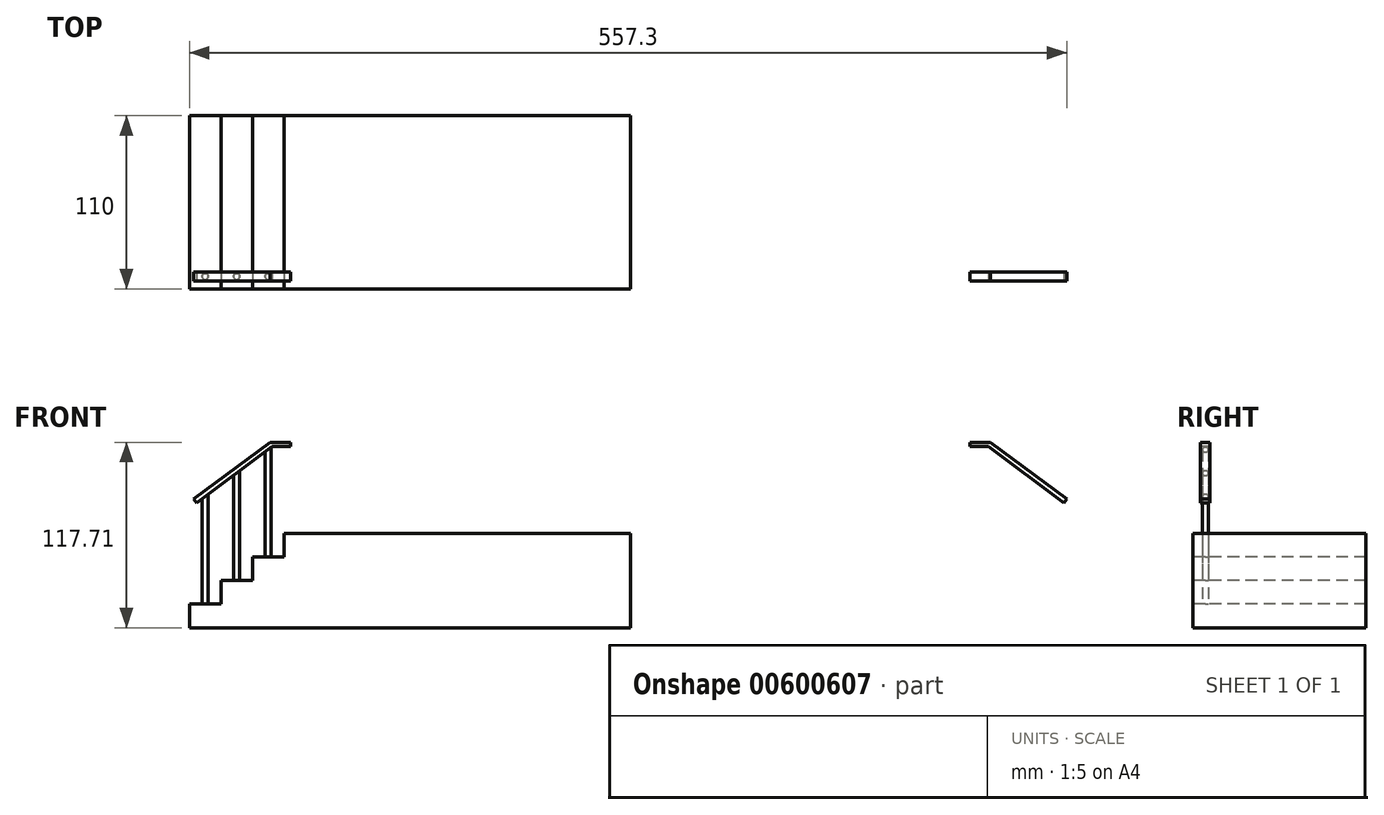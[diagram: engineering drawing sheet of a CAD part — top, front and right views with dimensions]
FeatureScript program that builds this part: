
annotation { "Feature Type Name" : "Feature", "Feature Type Description" : "" }
export const myFeature = defineFeature(function(context is Context, id is Id, definition is map)
    precondition{}
    {
        {
            var Q0;
            Q0=qCreatedBy(makeId("Top.planeOp"),FACE);
            var sketch = newSketch(context, id + "F0", { "sketchPlane" : qUnion([Q0])});
            skLineSegment(sketch, "E0.bottom", {"start": v(-214.98, -22.54) * mm, "end": v(5.02, -22.54) * mm});
            skLineSegment(sketch, "E0.top", {"start": v(-214.98, -132.54) * mm, "end": v(5.02, -132.54) * mm});
            skLineSegment(sketch, "E0.left", {"start": v(-214.98, -22.54) * mm, "end": v(-214.98, -132.54) * mm});
            skLineSegment(sketch, "E0.right", {"start": v(5.02, -22.54) * mm, "end": v(5.02, -132.54) * mm});
            skLineSegment(sketch, "E1.bottom", {"start": v(-214.98, -22.54) * mm, "end": v(-234.98, -22.54) * mm});
            skLineSegment(sketch, "E1.top", {"start": v(-214.98, -132.54) * mm, "end": v(-234.98, -132.54) * mm});
            skLineSegment(sketch, "E1.right", {"start": v(-234.98, -22.54) * mm, "end": v(-234.98, -132.54) * mm});
            skLineSegment(sketch, "E2.bottom", {"start": v(-234.98, -22.54) * mm, "end": v(-254.98, -22.54) * mm});
            skLineSegment(sketch, "E2.top", {"start": v(-234.98, -132.54) * mm, "end": v(-254.98, -132.54) * mm});
            skLineSegment(sketch, "E2.right", {"start": v(-254.98, -22.54) * mm, "end": v(-254.98, -132.54) * mm});
            skLineSegment(sketch, "E3.bottom", {"start": v(-254.98, -22.54) * mm, "end": v(-274.98, -22.54) * mm});
            skLineSegment(sketch, "E3.top", {"start": v(-254.98, -132.54) * mm, "end": v(-274.98, -132.54) * mm});
            skLineSegment(sketch, "E3.right", {"start": v(-274.98, -22.54) * mm, "end": v(-274.98, -132.54) * mm});
            skCircle(sketch, "E4", {"center": v(-264.98, -124.54) * mm, "radius": 2 * mm});
            skPoint(sketch, "E4.centerSnap0", {"position": v(-264.98, -132.54) * mm});
            skCircle(sketch, "E5", {"center": v(-244.98, -124.54) * mm, "radius": 2 * mm});
            skPoint(sketch, "E5.centerSnap0", {"position": v(-244.98, -132.54) * mm});
            skCircle(sketch, "E6", {"center": v(-224.98, -124.54) * mm, "radius": 2 * mm});
            skPoint(sketch, "E6.centerSnap0", {"position": v(-224.98, -132.54) * mm});
            skSolve(sketch);
        }
        {
            var Q0;
            Q0=makeQuery(id+"F0.imprint","IMPRINT",FACE,{"disambiguationData":[TD([[makeQuery(id+"F0.imprint","IMPRINT",EDGE,{"derivedFrom":sQuery(id+"F0.wireOp",EDGE,"E3.bottom")}),1.0]])]});
            extrude(context, id + "F1", {"entities" : qUnion([Q0]), "depth" : 15 * mm, "offsetDistance" : 25 * mm});
        }
        {
            var Q0;
            Q0=makeQuery(id+"F0.imprint","IMPRINT",FACE,{"disambiguationData":[TD([[makeQuery(id+"F0.imprint","IMPRINT",EDGE,{"derivedFrom":sQuery(id+"F0.wireOp",EDGE,"E2.bottom")}),1.0]])]});
            var Q1;
            Q1=makeQuery(id+"F0.imprint","IMPRINT",FACE,{"disambiguationData":[TD([[makeQuery(id+"F0.imprint","IMPRINT",EDGE,{"derivedFrom":sQuery(id+"F0.wireOp",EDGE,"E5")}),1.0]])]});
            extrude(context, id + "F2", {"entities" : qUnion([Q0, Q1]), "operationType" : NewBodyOperationType.ADD, "depth" : 30 * mm, "offsetDistance" : 25 * mm});
        }
        {
            var Q0;
            Q0=makeQuery(id+"F0.imprint","IMPRINT",FACE,{"disambiguationData":[TD([[makeQuery(id+"F0.imprint","IMPRINT",EDGE,{"derivedFrom":sQuery(id+"F0.wireOp",EDGE,"E1.bottom")}),1.0]])]});
            extrude(context, id + "F3", {"entities" : qUnion([Q0]), "operationType" : NewBodyOperationType.ADD, "depth" : 45 * mm, "offsetDistance" : 25 * mm});
        }
        {
            var Q0;
            Q0=makeQuery(id+"F0.imprint","IMPRINT",FACE,{"disambiguationData":[TD([[makeQuery(id+"F0.imprint","IMPRINT",EDGE,{"derivedFrom":sQuery(id+"F0.wireOp",EDGE,"E0.bottom")}),-1.0]])]});
            extrude(context, id + "F4", {"entities" : qUnion([Q0]), "operationType" : NewBodyOperationType.ADD, "depth" : 60 * mm, "offsetDistance" : 25 * mm});
        }
        {
            var Q0;
            Q0=makeQuery(id+"F0.imprint","IMPRINT",FACE,{"disambiguationData":[TD([[makeQuery(id+"F0.imprint","IMPRINT",EDGE,{"derivedFrom":sQuery(id+"F0.wireOp",EDGE,"E4")}),1.0]])]});
            extrude(context, id + "F5", {"entities" : qUnion([Q0]), "operationType" : NewBodyOperationType.ADD, "depth" : 85 * mm, "offsetDistance" : 25 * mm});
        }
        {
            var Q0;
            Q0=makeQuery(id+"F0.imprint","IMPRINT",FACE,{"disambiguationData":[TD([[makeQuery(id+"F0.imprint","IMPRINT",EDGE,{"derivedFrom":sQuery(id+"F0.wireOp",EDGE,"E5")}),1.0]])]});
            extrude(context, id + "F6", {"entities" : qUnion([Q0]), "operationType" : NewBodyOperationType.ADD, "depth" : 100 * mm, "offsetDistance" : 25 * mm});
        }
        {
            var Q0;
            Q0=makeQuery(id+"F0.imprint","IMPRINT",FACE,{"disambiguationData":[TD([[makeQuery(id+"F0.imprint","IMPRINT",EDGE,{"derivedFrom":sQuery(id+"F0.wireOp",EDGE,"E6")}),1.0]])]});
            extrude(context, id + "F7", {"entities" : qUnion([Q0]), "operationType" : NewBodyOperationType.ADD, "depth" : 115 * mm, "offsetDistance" : 25 * mm});
        }
        {
            var Q0;
            Q0=makeQuery(id+"F4.boolean.opBoolean","MERGE",FACE,{"derivedFrom":[makeQuery(id+"F3.boolean.opBoolean","MERGE",FACE,{"derivedFrom":[makeQuery(id+"F2.boolean.opBoolean","MERGE",FACE,{"derivedFrom":[makeQuery(id+"F1.opExtrude","SWEPT_FACE",FACE,{"disambiguationData":[OSD([sQuery(id+"F0.wireOp",EDGE,"E3.top")])]}),makeQuery(id+"F2.opExtrude","SWEPT_FACE",FACE,{"disambiguationData":[OSD([sQuery(id+"F0.wireOp",EDGE,"E2.top")])]})]}),makeQuery(id+"F3.opExtrude","SWEPT_FACE",FACE,{"disambiguationData":[OSD([sQuery(id+"F0.wireOp",EDGE,"E1.top")])]})]}),makeQuery(id+"F4.opExtrude","SWEPT_FACE",FACE,{"disambiguationData":[OSD([sQuery(id+"F0.wireOp",EDGE,"E0.top")])]})]});
            var sketch = newSketch(context, id + "F8", { "sketchPlane" : qUnion([Q0])});
            skLineSegment(sketch, "E7", {"start": v(-270.3, 79.25) * mm, "end": v(-222.4, 115.03) * mm});
            skLineSegment(sketch, "E8", {"start": v(-222.4, 115.03) * mm, "end": v(-210.7, 115.03) * mm});
            skLineSegment(sketch, "E9", {"start": v(-210.7, 115.03) * mm, "end": v(-210.7, 117.71) * mm});
            skLineSegment(sketch, "E10", {"start": v(-210.7, 117.71) * mm, "end": v(-223.86, 117.71) * mm});
            skLineSegment(sketch, "E11", {"start": v(-223.86, 117.71) * mm, "end": v(-272.28, 81.68) * mm});
            skLineSegment(sketch, "E12", {"start": v(-272.28, 81.68) * mm, "end": v(-270.3, 79.25) * mm});
            skSolve(sketch);
        }
        {
            var Q0;
            Q0=makeQuery(id+"F8.imprint","IMPRINT",FACE,{"disambiguationData":[TD([[makeQuery(id+"F8.imprint","IMPRINT",EDGE,{"derivedFrom":sQuery(id+"F8.wireOp",EDGE,"E7")}),1.0]])]});
            extrude(context, id + "F9", {"entities" : qUnion([Q0]), "operationType" : NewBodyOperationType.ADD, "oppositeDirection" : true, "depth" : 6 * mm, "offsetDistance" : 25 * mm});
        }
        {
            var Q0;
            Q0=makeQuery(id+"F9.opExtrude","SWEPT_BODY",BODY,{"disambiguationData":[OSD([sQuery(id+"F8.wireOp",EDGE,"E7"),sQuery(id+"F8.wireOp",EDGE,"E8"),sQuery(id+"F8.wireOp",EDGE,"E9"),sQuery(id+"F8.wireOp",EDGE,"E10"),sQuery(id+"F8.wireOp",EDGE,"E11"),sQuery(id+"F8.wireOp",EDGE,"E12")])]});
            transform(context, id + "F10", {"entities" : qUnion([Q0]), "transformType" : TransformType.TRANSLATION_3D, "dx" : 0 * mm, "dy" : 4.9 * mm, "dz" : 0 * mm, "makeCopy" : false});
        }
        {
            var Q0;
            Q0=makeQuery(id+"F9.opExtrude","SWEPT_BODY",BODY,{"disambiguationData":[OSD([sQuery(id+"F8.wireOp",EDGE,"E7"),sQuery(id+"F8.wireOp",EDGE,"E8"),sQuery(id+"F8.wireOp",EDGE,"E9"),sQuery(id+"F8.wireOp",EDGE,"E10"),sQuery(id+"F8.wireOp",EDGE,"E11"),sQuery(id+"F8.wireOp",EDGE,"E12")])]});
            var Q1;
            Q1=makeQuery(id+"F4.opExtrude","SWEPT_FACE",FACE,{"disambiguationData":[OSD([sQuery(id+"F0.wireOp",EDGE,"E0.right")])]});
            mirror(context, id + "F11", {"operationType" : NewBodyOperationType.ADD, "entities" : qUnion([Q0]), "mirrorPlane" : qUnion([Q1])});
        }
    });
